# Revit family: Reece_Accessory_Posh_Domaine_Heated Towel Rail_600 mm
name_source: partatom
category: Plumbing Fixtures
revit_build: Autodesk Revit 2018 (Build: 20190510_1515(x64)
units: mm (PartAtom-declared; Revit-internal decimal feet)

## family parameters
Cut with Voids When Loaded = Yes
Host = Face
Part Type = Normal
Room Calculation Point = No
Round Connector Dimension = Use Diameter
Shared = Yes

## types (1)
- 750 mm x 600 mm_Stainless Steel
    Default Elevation = 0 mm  [stored 0 ft]
    Description = Posh Domaine Heated Towel Rail 750 x 600mm Polished Stainless Steel
    Disclaimer = THIS FILE IS THE PROPERTY OF THE REECE GROUP. IT MAY NOT BE REPRODUCED, REVERSE-ENGINEERED OR MODIFIED. ANY REPUBLICATION, TRANSMISSION OR DISTRIBUTION FOR THE PURPOSE OF COMMERCIALLY EXPLOITING THE FILES IS PROHIBITED.
    Keynote = Product #9508098, Reece_Accessory_Posh_Domaine_Heated Towel Rail_600 mm - 750 mm x 600 mm_Stainless Steel
    Manufacturer = Posh
    Model = Domaine
    Reece_Detail_Additional = Heated Towel Rail
    Reece_Detail_Disclaimer = THIS FILE IS THE PROPERTY OF THE REECE GROUP. IT MAY NOT BE REPRODUCED, REVERSE-ENGINEERED OR MODIFIED. ANY REPUBLICATION, TRANSMISSION OR DISTRIBUTION FOR THE PURPOSE OF COMMERCIALLY EXPLOITING THE FILES IS PROHIBITED.
    Reece_Material_Main = Reece_Metal_Stainless Steel_Polished
    Reece_Overall_Height = 600 mm
    Reece_Overall_Projection = 112 mm  [stored 0.367454 ft]
    Reece_Overall_Width = 750 mm  [stored 2.46063 ft]
    Reece_Product_Brand = Posh
    Reece_Product_Description = Posh Domaine Heated Towel Rail 750 x 600mm Polished Stainless Steel
    Reece_Product_Mount = Wall Mounted
    Reece_Product_Number = 9508098
    Reece_Product_Sub Brand = Domaine
    Reece_Product_Type = Accessory
    Reece_Product_Web Page = https://www.reece.com.au
    Type Comments = Accessory
    URL = https://www.reece.com.au

note: [stored X ft] marks values corroborated as IEEE doubles in the binary element streams (Revit-internal decimal feet)

## geometry (parser evidence)
native form markers: Sweep x1
no freeform markers — native parametric forms only
